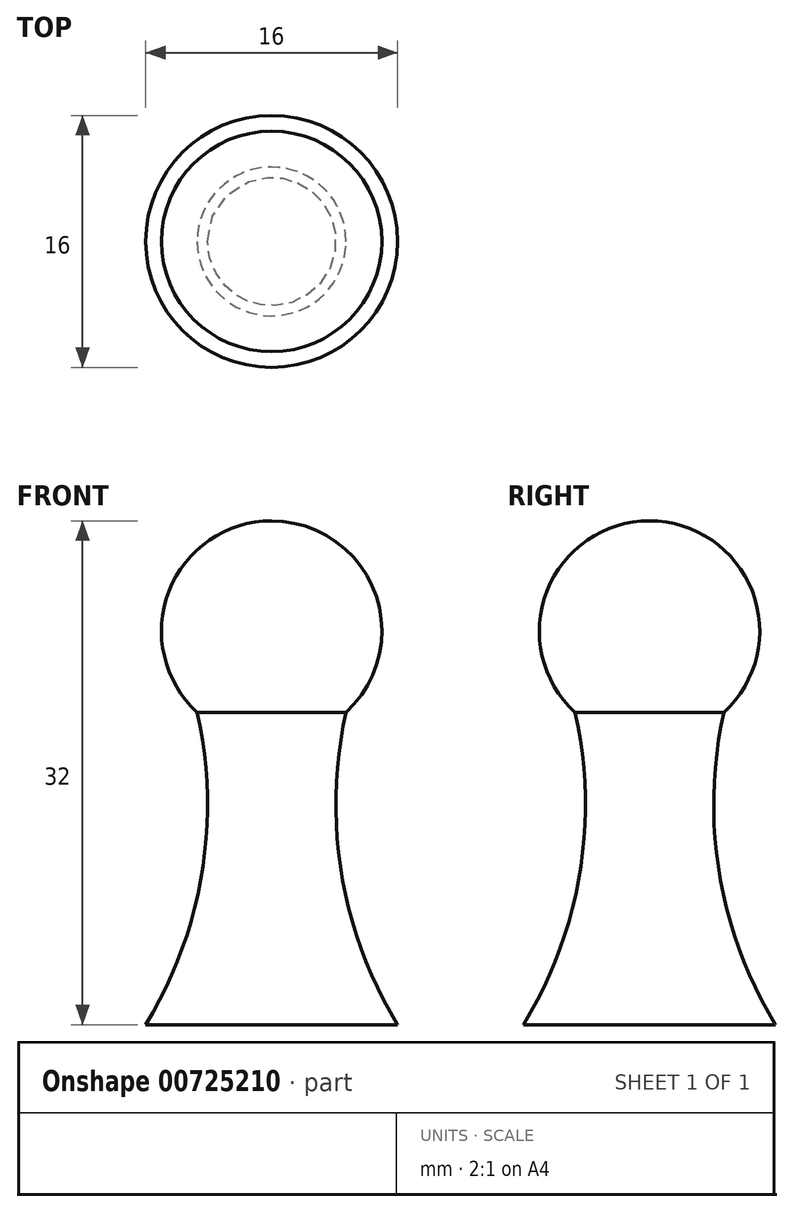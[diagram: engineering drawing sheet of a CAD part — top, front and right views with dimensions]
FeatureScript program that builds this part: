
annotation { "Feature Type Name" : "Feature", "Feature Type Description" : "" }
export const myFeature = defineFeature(function(context is Context, id is Id, definition is map)
    precondition{}
    {
        {
            var Q0;
            Q0=qCreatedBy(makeId("Front.planeOp"),FACE);
            var sketch = newSketch(context, id + "F0", { "sketchPlane" : qUnion([Q0])});
            skArc(sketch, "E0", {"start": v(0, 32) * mm, "mid": v(-6.52, 27.54) * mm, "end": v(-4.73, 19.84) * mm});
            skLineSegment(sketch, "E1", {"start": v(0, 0) * mm, "end": v(-8, 0) * mm});
            skArc(sketch, "E2", {"start": v(-8, 0) * mm, "mid": v(-4.43, 9.6) * mm, "end": v(-4.73, 19.84) * mm});
            skLineSegment(sketch, "E3", {"start": v(0, 0) * mm, "end": v(0, 32) * mm});
            skSolve(sketch);
        }
        {
            var Q0;
            Q0 = qSketchRegion(id + "F0", true);
            var Q1;
            Q1=sQuery(id+"F0.wireOp",EDGE,"E3");
            revolve(context, id + "F1", {"surfaceOperationType" : NewSurfaceOperationType.NEW, "entities" : qUnion([Q0]), "axis" : qUnion([Q1]), "revolveType" : RevolveType.FULL});
        }
    });
